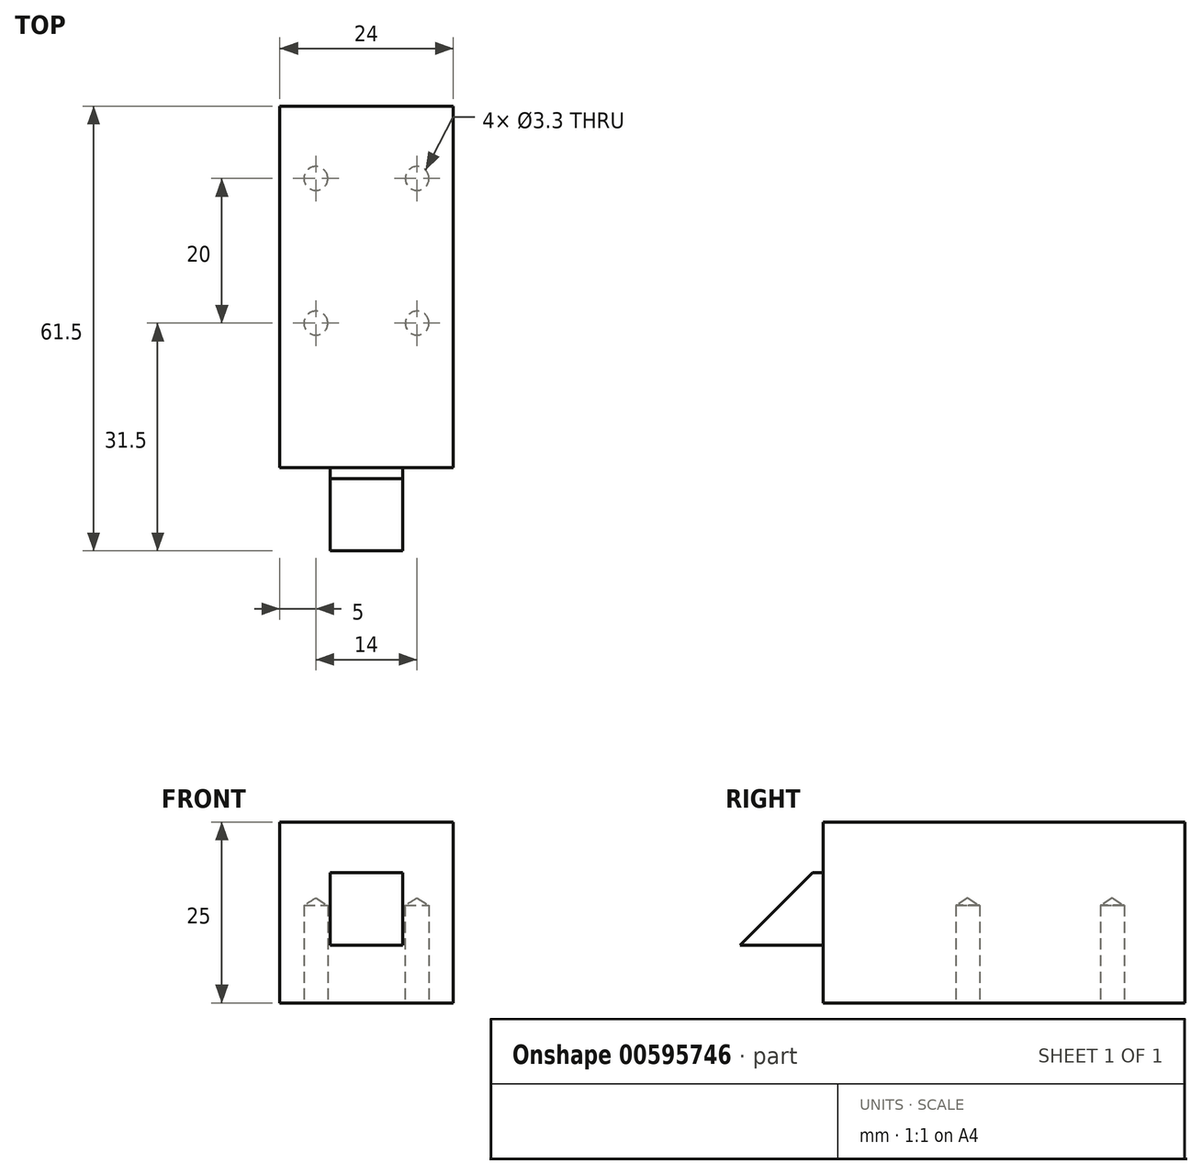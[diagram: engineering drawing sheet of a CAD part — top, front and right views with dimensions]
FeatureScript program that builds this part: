
annotation { "Feature Type Name" : "Feature", "Feature Type Description" : "" }
export const myFeature = defineFeature(function(context is Context, id is Id, definition is map)
    precondition{}
    {
        {
            var Q0;
            Q0=qCreatedBy(makeId("Front.planeOp"),FACE);
            var sketch = newSketch(context, id + "F0", { "sketchPlane" : qUnion([Q0])});
            skLineSegment(sketch, "E0", {"start": v(21, 0) * mm, "end": v(21, 1) * mm});
            skLineSegment(sketch, "E1", {"start": v(21, 1) * mm, "end": v(12, 1) * mm});
            skLineSegment(sketch, "E2", {"start": v(12, 1) * mm, "end": v(12, 28) * mm});
            skLineSegment(sketch, "E3", {"start": v(12, 28) * mm, "end": v(0, 28) * mm});
            skLineSegment(sketch, "E4", {"start": v(0, 28) * mm, "end": v(0, 0) * mm});
            skLineSegment(sketch, "E5", {"start": v(0, 0) * mm, "end": v(21, 0) * mm});
            skSolve(sketch);
        }
        {
            var Q0;
            Q0=makeQuery(id+"F0.imprint","IMPRINT",FACE,{"disambiguationData":[TD([[makeQuery(id+"F0.imprint","IMPRINT",EDGE,{"derivedFrom":sQuery(id+"F0.wireOp",EDGE,"E0")}),1.0]])]});
            extrude(context, id + "F1", {"entities" : qUnion([Q0]), "oppositeDirection" : true, "depth" : 50 * mm, "offsetDistance" : 25 * mm});
        }
        {
            var Q0;
            Q0=makeQuery(id+"F1.opExtrude","SWEPT_BODY",BODY,{"disambiguationData":[OSD([sQuery(id+"F0.wireOp",EDGE,"E0"),sQuery(id+"F0.wireOp",EDGE,"E1"),sQuery(id+"F0.wireOp",EDGE,"E2"),sQuery(id+"F0.wireOp",EDGE,"E3"),sQuery(id+"F0.wireOp",EDGE,"E4"),sQuery(id+"F0.wireOp",EDGE,"E5")])]});
            var Q1;
            Q1=qCreatedBy(makeId("Right.planeOp"),FACE);
            mirror(context, id + "F2", {"operationType" : NewBodyOperationType.ADD, "entities" : qUnion([Q0]), "mirrorPlane" : qUnion([Q1])});
        }
        {
            var Q0;
            Q0=qCreatedBy(makeId("Right.planeOp"),FACE);
            var sketch = newSketch(context, id + "F3", { "sketchPlane" : qUnion([Q0])});
            skLineSegment(sketch, "E6", {"start": v(-1.5, 18) * mm, "end": v(-11.5, 8) * mm});
            skLineSegment(sketch, "E7", {"start": v(-11.5, 8) * mm, "end": v(0, 8) * mm});
            skLineSegment(sketch, "E8", {"start": v(0, 8) * mm, "end": v(0, 18) * mm});
            skLineSegment(sketch, "E9", {"start": v(0, 18) * mm, "end": v(-1.5, 18) * mm});
            skSolve(sketch);
        }
        {
            var Q0;
            Q0=makeQuery(id+"F3.imprint","IMPRINT",FACE,{"disambiguationData":[TD([[makeQuery(id+"F3.imprint","IMPRINT",EDGE,{"derivedFrom":sQuery(id+"F3.wireOp",EDGE,"E6")}),1.0]])]});
            extrude(context, id + "F4", {"entities" : qUnion([Q0]), "operationType" : NewBodyOperationType.ADD, "depth" : 10 * mm, "offsetDistance" : 25 * mm, "symmetric" : true});
        }
        {
            var Q0;
            {var subQ0=makeQuery(id+"F1.opExtrude","SWEPT_FACE",FACE,{"disambiguationData":[OSD([sQuery(id+"F0.wireOp",EDGE,"E5")])]});Q0=makeQuery(id+"F2.boolean.opBoolean","MERGE",FACE,{"derivedFrom":[subQ0,makeQuery(id+"F2.opPattern","COPY",FACE,{"derivedFrom":subQ0,"instanceName":"1"})]});}
            var sketch = newSketch(context, id + "F5", { "sketchPlane" : qUnion([Q0])});
            skLineSegment(sketch, "E10.top", {"start": v(-12, -50) * mm, "end": v(12, -50) * mm});
            skLineSegment(sketch, "E10.left", {"start": v(-12, 0) * mm, "end": v(-12, -50) * mm});
            skLineSegment(sketch, "E10.right", {"start": v(12, 0) * mm, "end": v(12, -50) * mm});
            skLineSegment(sketch, "E11.0", {"start": v(-12, 0) * mm, "end": v(-12, -50) * mm, "construction": true});
            skLineSegment(sketch, "E12.0", {"start": v(12, -50) * mm, "end": v(12, 0) * mm, "construction": true});
            skLineSegment(sketch, "E13", {"start": v(-12, 0) * mm, "end": v(-12, 11.5) * mm});
            skLineSegment(sketch, "E14", {"start": v(12, 0) * mm, "end": v(12, 11.5) * mm});
            skLineSegment(sketch, "E15", {"start": v(12, 11.5) * mm, "end": v(-12, 11.5) * mm});
            skSolve(sketch);
        }
        {
            var Q0;
            Q0 = qSketchRegion(id + "F5", true);
            extrude(context, id + "F6", {"entities" : qUnion([Q0]), "operationType" : NewBodyOperationType.INTERSECT, "oppositeDirection" : true, "depth" : 25 * mm, "offsetDistance" : 25 * mm});
        }
        {
            var Q0;
            {var subQ0=makeQuery(id+"F1.opExtrude","SWEPT_FACE",FACE,{"disambiguationData":[OSD([sQuery(id+"F0.wireOp",EDGE,"E5")])]});Q0=makeQuery(id+"F2.boolean.opBoolean","MERGE",FACE,{"derivedFrom":[subQ0,makeQuery(id+"F2.opPattern","COPY",FACE,{"derivedFrom":subQ0,"instanceName":"1"})]});}
            var sketch = newSketch(context, id + "F7", { "sketchPlane" : qUnion([Q0])});
            skLineSegment(sketch, "E16.bottom", {"start": v(7, -20) * mm, "end": v(-7, -20) * mm, "construction": true});
            skLineSegment(sketch, "E16.top", {"start": v(7, -40) * mm, "end": v(-7, -40) * mm, "construction": true});
            skLineSegment(sketch, "E16.left", {"start": v(7, -20) * mm, "end": v(7, -40) * mm, "construction": true});
            skLineSegment(sketch, "E16.right", {"start": v(-7, -20) * mm, "end": v(-7, -40) * mm, "construction": true});
            skPoint(sketch, "E16.middle", {"position": v(0, -30) * mm});
            skPoint(sketch, "E17", {"position": v(7, -20) * mm});
            skPoint(sketch, "E18", {"position": v(7, -40) * mm});
            skPoint(sketch, "E19", {"position": v(-7, -40) * mm});
            skPoint(sketch, "E20", {"position": v(-7, -20) * mm});
            skSolve(sketch);
        }
        {
            var Q0;
            Q0=sQuery(id+"F7.wireOp",VERTEX,"E17");
            var Q1;
            Q1=sQuery(id+"F7.wireOp",VERTEX,"E18");
            var Q2;
            Q2=sQuery(id+"F7.wireOp",VERTEX,"E19");
            var Q3;
            Q3=sQuery(id+"F7.wireOp",VERTEX,"E20");
            var Q4;
            Q4=makeQuery(id+"F1.opExtrude","SWEPT_BODY",BODY,{"disambiguationData":[OSD([sQuery(id+"F0.wireOp",EDGE,"E0"),sQuery(id+"F0.wireOp",EDGE,"E1"),sQuery(id+"F0.wireOp",EDGE,"E2"),sQuery(id+"F0.wireOp",EDGE,"E3"),sQuery(id+"F0.wireOp",EDGE,"E4"),sQuery(id+"F0.wireOp",EDGE,"E5")])]});
            hole(context, id + "F8", {"style" : HoleStyle.SIMPLE, "endStyle" : HoleEndStyle.BLIND, "standardTappedOrClearance" : lookupTablePath({ "standard" : "ISO", "fit" : "Normal", "size" : "M3", "type" : "Clearance" }), "standardBlindInLast" : lookupTablePath({ "fit" : "Standard", "standard" : "ISO", "size" : "M3", "type" : "Clearance" }), "holeDiameter" : 3.3 * mm, "majorDiameter" : 3 * mm, "holeDepth" : 13.5 * mm, "isTappedThrough" : true, "tappedDepth" : 12 * mm, "tapClearance" : 3, "locations" : qUnion([Q0, Q1, Q2, Q3]), "scope" : qUnion([Q4])});
        }
    });
